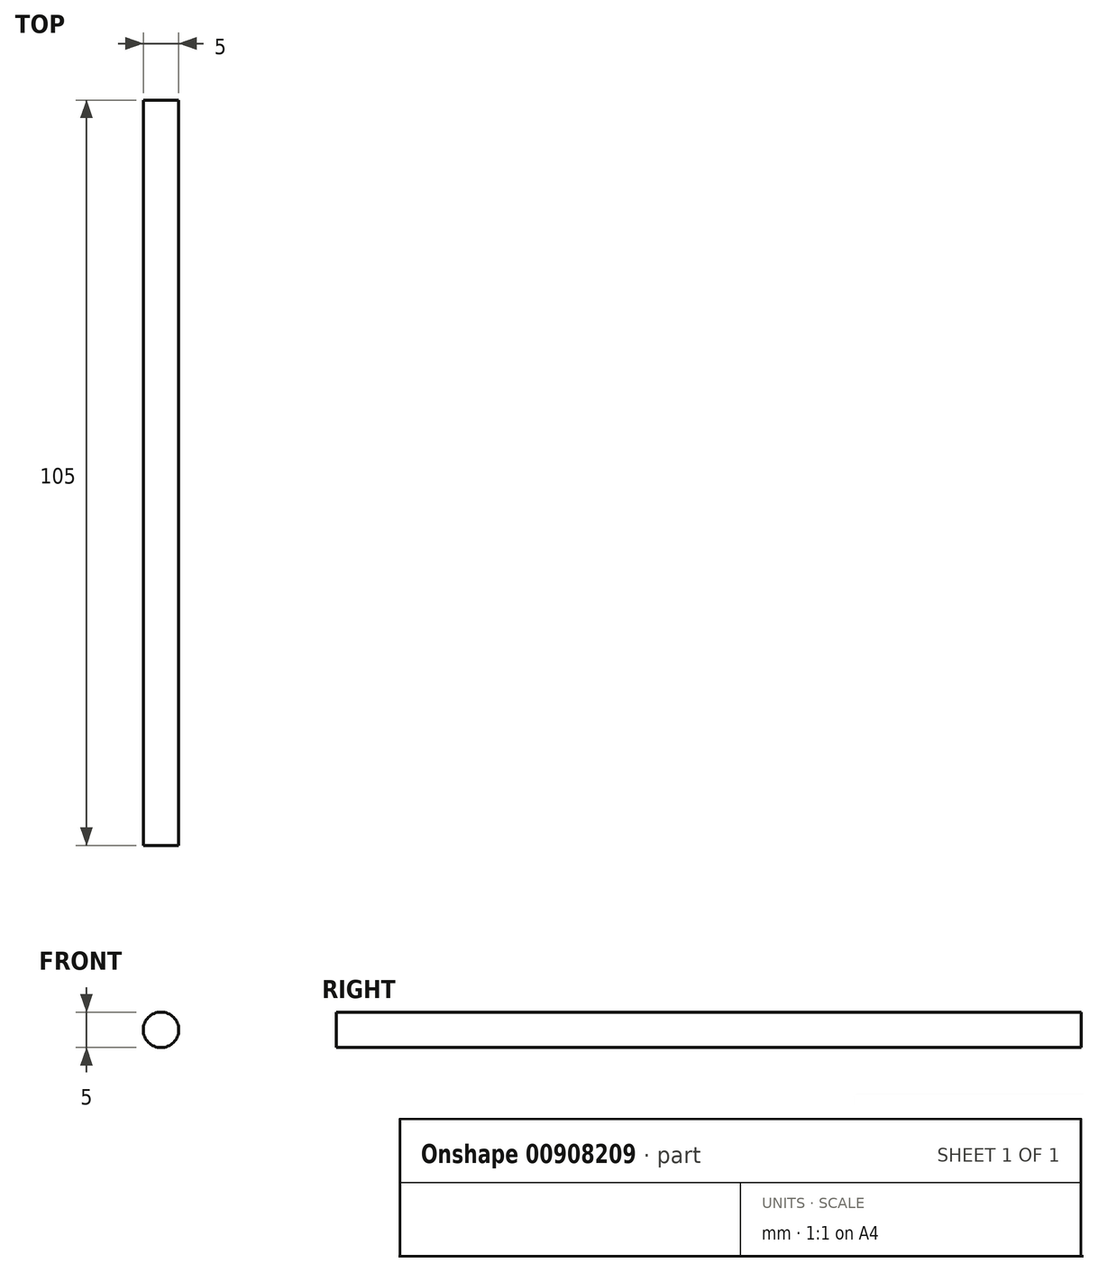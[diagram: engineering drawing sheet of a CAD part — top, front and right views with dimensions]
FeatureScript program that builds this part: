
annotation { "Feature Type Name" : "Feature", "Feature Type Description" : "" }
export const myFeature = defineFeature(function(context is Context, id is Id, definition is map)
    precondition{}
    {
        {
            var Q0;
            Q0=qCreatedBy(makeId("Front.planeOp"),FACE);
            var sketch = newSketch(context, id + "F0", { "sketchPlane" : qUnion([Q0])});
            skCircle(sketch, "E0", {"center": v(0, 0) * mm, "radius": 2.5 * mm});
            skSolve(sketch);
        }
        {
            var Q0;
            Q0=makeQuery(id+"F0.imprint","IMPRINT",FACE,{"disambiguationData":[TD([[makeQuery(id+"F0.imprint","IMPRINT",EDGE,{"derivedFrom":sQuery(id+"F0.wireOp",EDGE,"E0")}),1.0]])]});
            extrude(context, id + "F1", {"entities" : qUnion([Q0]), "depth" : 105 * mm, "offsetDistance" : 25 * mm, "symmetric" : true});
        }
    });
